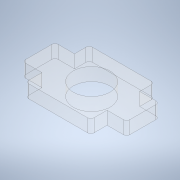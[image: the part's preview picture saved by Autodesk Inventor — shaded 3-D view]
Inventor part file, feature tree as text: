
AUTODESK INVENTOR PART (.ipt)
format: ipt  version: 2021 (Build 250183000, 183)  size: 130,048 bytes
history: native  units: mm
features: extrude x1, sketch x1
ambient origin geometry x8: Origin, YZ Plane, XZ Plane, XY Plane, X Axis, Y Axis, Z Axis, Center Point
bodies: Solid1 (feature_tree)
feature tree (2):
  extrude  "Extrusion1"  Depth=1.0mm
  sketch  "Sketch1"  dims[d5=1.0mm d6=1.0mm d7=4.0mm d8=0.0mm d9=1.0mm d10=11.3mm]
